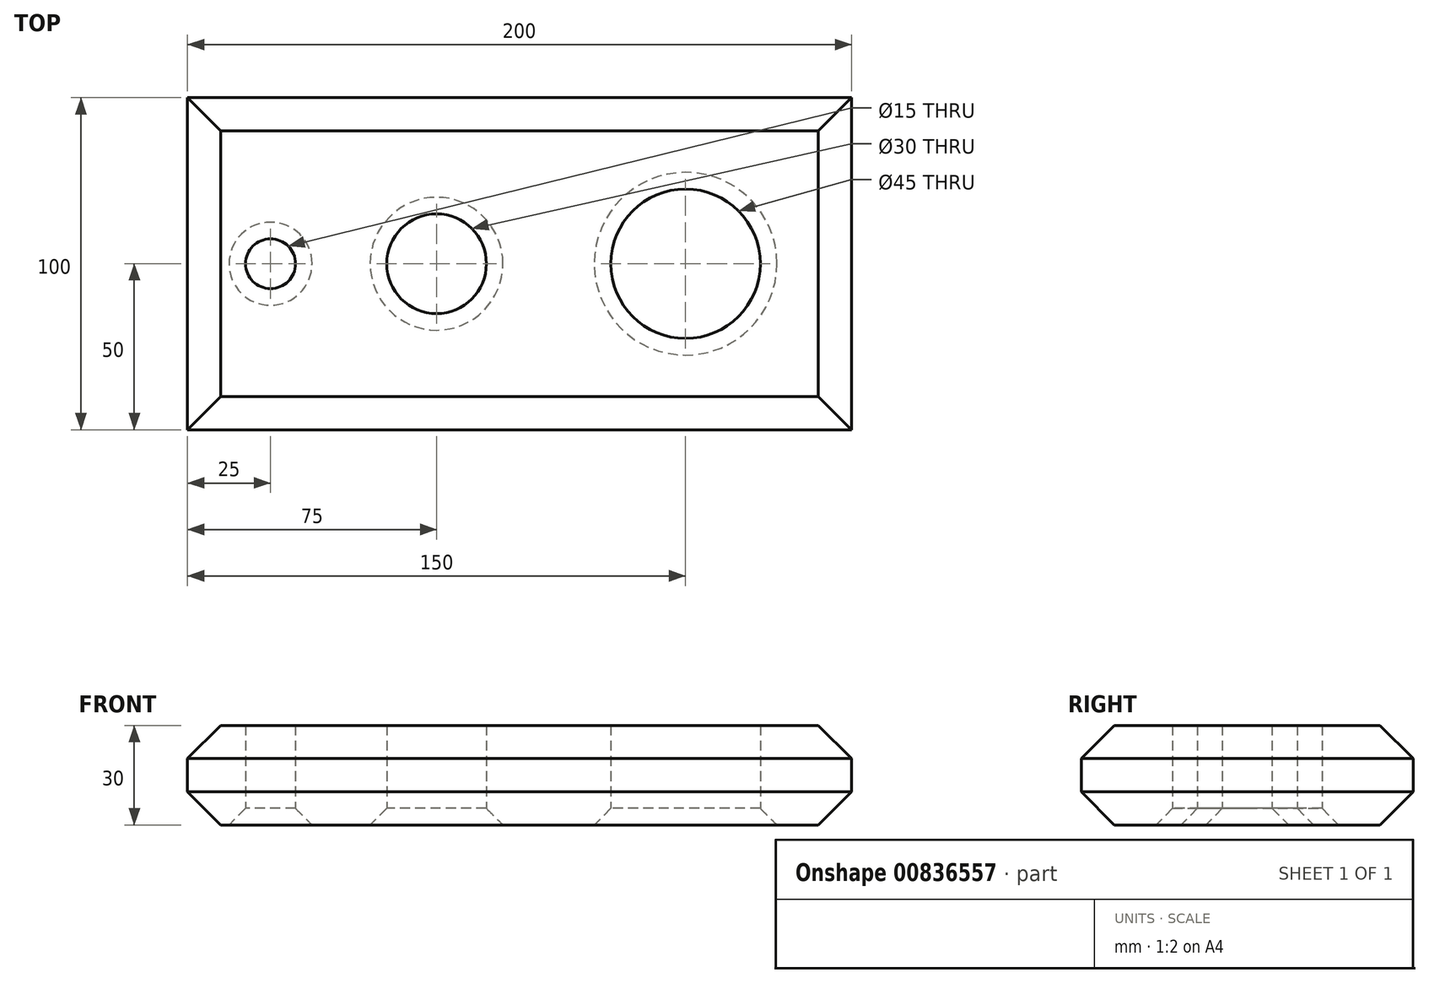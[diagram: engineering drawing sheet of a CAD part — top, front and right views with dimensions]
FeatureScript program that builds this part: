
annotation { "Feature Type Name" : "Feature", "Feature Type Description" : "" }
export const myFeature = defineFeature(function(context is Context, id is Id, definition is map)
    precondition{}
    {
        {
            var Q0;
            Q0=qCreatedBy(makeId("Top.planeOp"),FACE);
            var sketch = newSketch(context, id + "F0", { "sketchPlane" : qUnion([Q0])});
            skLineSegment(sketch, "E0.bottom", {"start": v(-100, 50) * mm, "end": v(100, 50) * mm});
            skLineSegment(sketch, "E0.top", {"start": v(-100, -50) * mm, "end": v(100, -50) * mm});
            skLineSegment(sketch, "E0.left", {"start": v(-100, 50) * mm, "end": v(-100, -50) * mm});
            skLineSegment(sketch, "E0.right", {"start": v(100, 50) * mm, "end": v(100, -50) * mm});
            skCircle(sketch, "E1", {"center": v(-75, 0) * mm, "radius": 7.5 * mm});
            skCircle(sketch, "E2", {"center": v(-25, 0) * mm, "radius": 15 * mm});
            skCircle(sketch, "E3", {"center": v(50, 0) * mm, "radius": 22.5 * mm});
            skSolve(sketch);
        }
        {
            var Q0;
            Q0 = qSketchRegion(id + "F0", true);
            extrude(context, id + "F1", {"entities" : qUnion([Q0]), "depth" : 30 * mm, "offsetDistance" : 25 * mm});
        }
        {
            var Q0;
            Q0=makeQuery(id+"F1.opExtrude","CAP_EDGE",EDGE,{"disambiguationData":[OSD([sQuery(id+"F0.wireOp",EDGE,"E3")])],"isStart":true});
            chamfer(context, id + "F2", {"entities" : qUnion([Q0]), "chamferType" : ChamferType.OFFSET_ANGLE, "width" : 5 * mm, "oppositeDirection" : false, "angle" : 45 * degree, "tangentPropagation" : true});
        }
        {
            var Q0;
            Q0=makeQuery(id+"F1.opExtrude","CAP_EDGE",EDGE,{"disambiguationData":[OSD([sQuery(id+"F0.wireOp",EDGE,"E2")])],"isStart":true});
            chamfer(context, id + "F3", {"entities" : qUnion([Q0]), "chamferType" : ChamferType.OFFSET_ANGLE, "width" : 5 * mm, "oppositeDirection" : false, "angle" : 45 * degree, "tangentPropagation" : true});
        }
        {
            var Q0;
            Q0=makeQuery(id+"F1.opExtrude","CAP_EDGE",EDGE,{"disambiguationData":[OSD([sQuery(id+"F0.wireOp",EDGE,"E1")])],"isStart":true});
            chamfer(context, id + "F4", {"entities" : qUnion([Q0]), "chamferType" : ChamferType.OFFSET_ANGLE, "width" : 5 * mm, "oppositeDirection" : false, "angle" : 45 * degree, "tangentPropagation" : true});
        }
        {
            var Q0;
            Q0=makeQuery(id+"F1.opExtrude","CAP_EDGE",EDGE,{"disambiguationData":[OSD([sQuery(id+"F0.wireOp",EDGE,"E0.bottom")])],"isStart":true});
            var Q1;
            Q1=makeQuery(id+"F1.opExtrude","CAP_EDGE",EDGE,{"disambiguationData":[OSD([sQuery(id+"F0.wireOp",EDGE,"E0.left")])],"isStart":true});
            var Q2;
            Q2=makeQuery(id+"F1.opExtrude","CAP_EDGE",EDGE,{"disambiguationData":[OSD([sQuery(id+"F0.wireOp",EDGE,"E0.top")])],"isStart":true});
            var Q3;
            Q3=makeQuery(id+"F1.opExtrude","CAP_EDGE",EDGE,{"disambiguationData":[OSD([sQuery(id+"F0.wireOp",EDGE,"E0.right")])],"isStart":true});
            var Q4;
            Q4=makeQuery(id+"F1.opExtrude","CAP_EDGE",EDGE,{"disambiguationData":[OSD([sQuery(id+"F0.wireOp",EDGE,"E0.bottom")])],"isStart":false});
            var Q5;
            Q5=makeQuery(id+"F1.opExtrude","CAP_EDGE",EDGE,{"disambiguationData":[OSD([sQuery(id+"F0.wireOp",EDGE,"E0.right")])],"isStart":false});
            var Q6;
            Q6=makeQuery(id+"F1.opExtrude","CAP_EDGE",EDGE,{"disambiguationData":[OSD([sQuery(id+"F0.wireOp",EDGE,"E0.top")])],"isStart":false});
            var Q7;
            Q7=makeQuery(id+"F1.opExtrude","CAP_EDGE",EDGE,{"disambiguationData":[OSD([sQuery(id+"F0.wireOp",EDGE,"E0.left")])],"isStart":false});
            chamfer(context, id + "F5", {"entities" : qUnion([Q0, Q1, Q2, Q3, Q4, Q5, Q6, Q7]), "chamferType" : ChamferType.OFFSET_ANGLE, "width" : 10 * mm, "oppositeDirection" : false, "angle" : 45 * degree, "tangentPropagation" : true});
        }
    });
